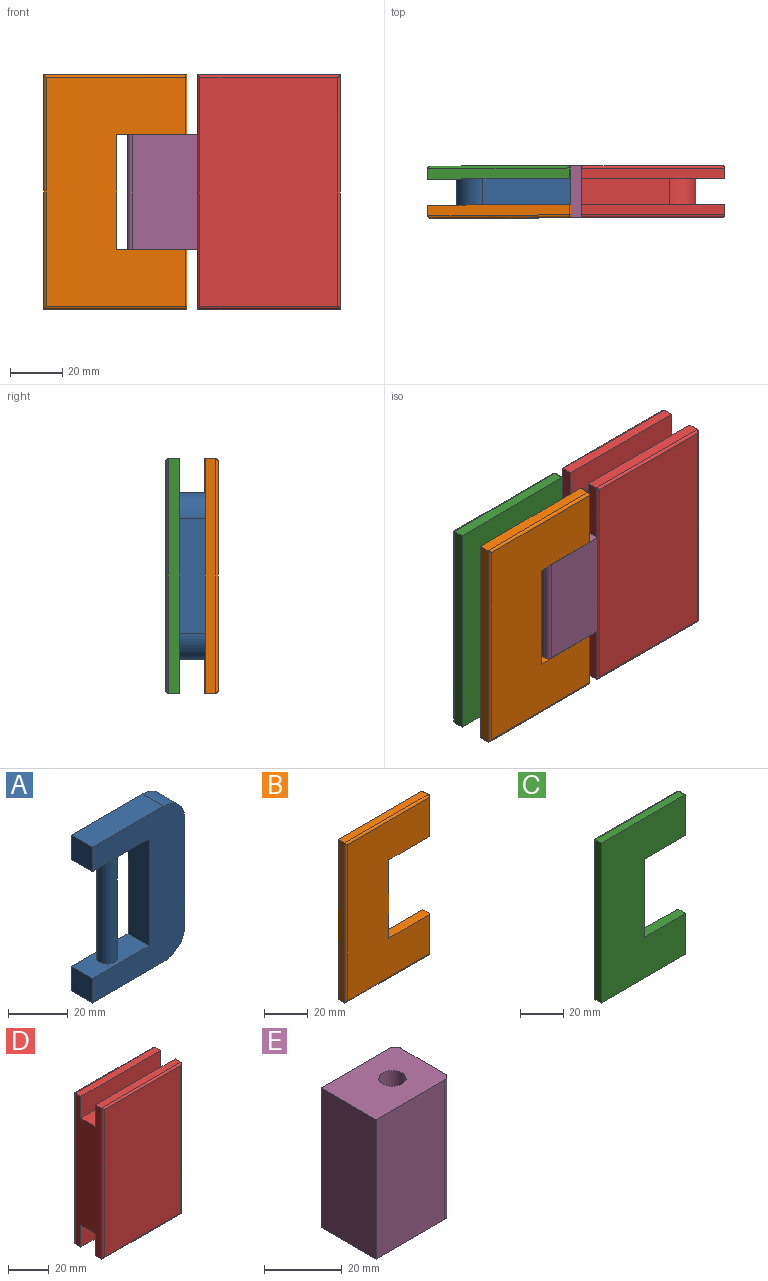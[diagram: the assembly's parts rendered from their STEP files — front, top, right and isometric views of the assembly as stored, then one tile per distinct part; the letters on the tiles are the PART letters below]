
ASSEMBLY  parts=5 mates=4
PART A: 13 faces, bbox 44x10x64 mm
  f0: plane 27x10mm, normal (0,0,-1), area 231.5mm2, adj f1,f9,f10,f11,f12
  f1: plane 44x10mm, normal (-1,0,0), area 440mm2, adj f0,f2,f10,f11
  f2: plane 27x10mm, normal (0,0,1), area 231.5mm2, adj f1,f3,f10,f11,f12
  f3: plane 10x10mm, normal (-1,0,0), area 100mm2, adj f2,f4,f10,f11
  f4: plane 34x10mm, normal (0,0,-1), area 340mm2, adj f3,f5,f10,f11
  f5: cylinder r=10mm len=10mm, axis (0,1,0), area 157.1mm2, adj f4,f6,f10,f11
  f6: plane 44x10mm, normal (1,0,0), area 440mm2, adj f5,f7,f10,f11
  f7: cylinder r=10mm len=10mm, axis (0,1,0), area 157.1mm2, adj f6,f8,f10,f11
  f8: plane 34x10mm, normal (0,0,1), area 340mm2, adj f7,f9,f10,f11
  f9: plane 10x10mm, normal (-1,0,0), area 100mm2, adj f0,f8,f10,f11
  f10: plane 64x44mm, normal (0,-1,0), area 1585.1mm2, adj f0,f1,f2,f3,f4,f5,f6,f7
  f11: plane 64x44mm, normal (0,1,0), area 1585.1mm2, adj f0,f1,f2,f3,f4,f5,f6,f7
  f12: cylinder r=3.5mm len=44mm, axis (0,0,-1), area 967.6mm2, adj f0,f2
PART B: 19 faces, bbox 55x5.1x90.2 mm
  f0: plane 90x4mm, normal (-1,0,0), area 360mm2, adj f1,f7,f9,f11
  f1: plane 54.5x4mm, normal (0,0,-1), area 218mm2, adj f0,f9,f12,f15
  f2: plane 22.5x4.5mm, normal (1,0,0), area 101.2mm2, adj f3,f9,f13,f14,f15
  f3: plane 27x5mm, normal (0,0,1), area 134.9mm2, adj f2,f4,f8,f9,f13
  f4: plane 44x5mm, normal (1,0,0), area 220mm2, adj f3,f5,f8,f9
  f5: plane 27x5mm, normal (0,0,-1), area 134.9mm2, adj f4,f6,f8,f9,f16
  f6: plane 22.5x4.5mm, normal (1,0,0), area 101.2mm2, adj f5,f9,f16,f17,f18
  f7: plane 54.5x4mm, normal (0,0,1), area 218mm2, adj f0,f9,f10,f18
  f8: plane 88x53.5mm, normal (0,-1,0), area 3542mm2, adj f3,f4,f5,f10,f11,f12,f13,f16
  f9: plane 90x55mm, normal (0,1,0), area 3761.9mm2, adj f0,f1,f2,f3,f4,f5,f6,f7
  f10: cylinder r=1mm len=54.5mm, axis (1,0,0), area 85mm2, adj f7,f8,f11,f17
  f11: cylinder r=1mm len=90mm, axis (0,0,1), area 140.2mm2, adj f0,f8,f10,f12
  f12: cylinder r=1mm len=54.5mm, axis (-1,0,0), area 85mm2, adj f1,f8,f11,f14
  f13: cylinder r=0.5mm len=22mm, axis (0,0,-1), area 17.3mm2, adj f2,f3,f8,f14
  f14: torus R=0.5mm, axis (-1,0,0), area 1mm2, adj f2,f12,f13,f15
  f15: cylinder r=0.5mm len=4mm, axis (0,1,0), area 3.1mm2, adj f1,f2,f9,f14
  f16: cylinder r=0.5mm len=22mm, axis (0,0,-1), area 17.3mm2, adj f5,f6,f8,f17
  f17: torus R=0.5mm, axis (-1,0,0), area 1mm2, adj f6,f10,f16,f18
  f18: cylinder r=0.5mm len=4mm, axis (0,-1,0), area 3.1mm2, adj f6,f7,f9,f17
PART C: 19 faces, bbox 55x5.1x90.2 mm
  f0: plane 90x4mm, normal (-1,0,0), area 360mm2, adj f1,f7,f9,f11
  f1: plane 54.5x4mm, normal (0,0,-1), area 218mm2, adj f0,f9,f12,f15
  f2: plane 22.5x4.5mm, normal (1,0,0), area 101.2mm2, adj f3,f9,f13,f14,f15
  f3: plane 27x5mm, normal (0,0,1), area 134.9mm2, adj f2,f4,f8,f9,f13
  f4: plane 44x5mm, normal (1,0,0), area 220mm2, adj f3,f5,f8,f9
  f5: plane 27x5mm, normal (0,0,-1), area 134.9mm2, adj f4,f6,f8,f9,f16
  f6: plane 22.5x4.5mm, normal (1,0,0), area 101.2mm2, adj f5,f9,f16,f17,f18
  f7: plane 54.5x4mm, normal (0,0,1), area 218mm2, adj f0,f9,f10,f18
  f8: plane 88x53.5mm, normal (0,1,0), area 3542mm2, adj f3,f4,f5,f10,f11,f12,f13,f16
  f9: plane 90x55mm, normal (0,-1,0), area 3761.9mm2, adj f0,f1,f2,f3,f4,f5,f6,f7
  f10: cylinder r=1mm len=54.5mm, axis (1,0,0), area 85mm2, adj f7,f8,f11,f17
  f11: cylinder r=1mm len=90mm, axis (0,0,1), area 140.2mm2, adj f0,f8,f10,f12
  f12: cylinder r=1mm len=54.5mm, axis (-1,0,0), area 85mm2, adj f1,f8,f11,f14
  f13: cylinder r=0.5mm len=22mm, axis (0,0,-1), area 17.3mm2, adj f2,f3,f8,f14
  f14: torus R=0.5mm, axis (-1,0,0), area 1mm2, adj f2,f12,f13,f15
  f15: cylinder r=0.5mm len=4mm, axis (0,-1,0), area 3.1mm2, adj f1,f2,f9,f14
  f16: cylinder r=0.5mm len=22mm, axis (0,0,-1), area 17.3mm2, adj f5,f6,f8,f17
  f17: torus R=0.5mm, axis (-1,0,0), area 1mm2, adj f6,f10,f16,f18
  f18: cylinder r=0.5mm len=4mm, axis (0,1,0), area 3.1mm2, adj f6,f7,f9,f17
PART D: 24 faces, bbox 55x20x90 mm
  f0: plane 90x55mm, normal (0,1,0), area 2176.9mm2, adj f1,f2,f3,f4,f19,f20,f21,f22
  f1: plane 90x18mm, normal (-1,0,0), area 1360mm2, adj f0,f2,f4,f6,f10,f12,f14,f15
  f2: plane 55x4mm, normal (0,0,-1), area 220mm2, adj f0,f1,f3,f7
  f3: plane 90x4mm, normal (1,0,0), area 360mm2, adj f0,f2,f4,f9
  f4: plane 55x4mm, normal (0,0,1), area 220mm2, adj f0,f1,f3,f8
  f5: plane 88x53mm, normal (0,-1,0), area 4664mm2, adj f6,f7,f8,f9
  f6: cylinder r=1mm len=90mm, axis (0,0,1), area 140.2mm2, adj f1,f5,f7,f8
  f7: cylinder r=1mm len=55mm, axis (-1,0,0), area 85.3mm2, adj f2,f5,f6,f9
  f8: cylinder r=1mm len=55mm, axis (1,0,0), area 85.3mm2, adj f4,f5,f6,f9
  f9: cylinder r=1mm len=90mm, axis (0,0,-1), area 140.2mm2, adj f3,f5,f7,f8
  f10: plane 55x4mm, normal (0,0,-1), area 220mm2, adj f1,f11,f14,f16
  f11: plane 90x4mm, normal (1,0,0), area 360mm2, adj f10,f12,f14,f18
  f12: plane 55x4mm, normal (0,0,1), area 220mm2, adj f1,f11,f14,f17
  f13: plane 88x53mm, normal (0,1,0), area 4664mm2, adj f15,f16,f17,f18
  f14: plane 90x55mm, normal (0,-1,0), area 2176.9mm2, adj f1,f10,f11,f12,f19,f20,f21,f22
  f15: cylinder r=1mm len=90mm, axis (0,0,1), area 140.2mm2, adj f1,f13,f16,f17
  f16: cylinder r=1mm len=55mm, axis (-1,0,0), area 85.3mm2, adj f10,f13,f15,f18
  f17: cylinder r=1mm len=55mm, axis (1,0,0), area 85.3mm2, adj f12,f13,f15,f18
  f18: cylinder r=1mm len=90mm, axis (0,0,-1), area 140.2mm2, adj f11,f13,f16,f17
  f19: plane 34x10mm, normal (0,0,1), area 340mm2, adj f0,f1,f14,f23
  f20: plane 34x10mm, normal (0,0,-1), area 340mm2, adj f0,f1,f14,f21
  f21: cylinder r=10mm len=10mm, axis (0,1,0), area 157.1mm2, adj f0,f14,f20,f22
  f22: plane 44x10mm, normal (1,0,0), area 440mm2, adj f0,f14,f21,f23
  f23: cylinder r=10mm len=10mm, axis (0,1,0), area 157.1mm2, adj f0,f14,f19,f22
PART E: 9 faces, bbox 27x20x44 mm
  f0: plane 44x25mm, normal (0,1,0), area 1100mm2, adj f1,f5,f7,f8
  f1: plane 44x20mm, normal (-1,0,0), area 880mm2, adj f0,f2,f7,f8
  f2: plane 44x25mm, normal (0,-1,0), area 1100mm2, adj f1,f3,f7,f8
  f3: cylinder r=2mm len=44mm, axis (0,0,-1), area 138.2mm2, adj f2,f4,f7,f8
  f4: plane 44x16mm, normal (1,0,0), area 704mm2, adj f3,f5,f7,f8
  f5: cylinder r=2mm len=44mm, axis (0,0,-1), area 138.2mm2, adj f0,f4,f7,f8
  f6: cylinder r=3.5mm len=44mm, axis (0,0,-1), area 967.6mm2, adj f7,f8
  f7: plane 27x20mm, normal (0,0,1), area 499.8mm2, adj f0,f1,f2,f3,f4,f5,f6
  f8: plane 27x20mm, normal (0,0,-1), area 499.8mm2, adj f0,f1,f2,f3,f4,f5,f6
PLACE A rot(axis=(0,0,-1),179.7deg) t=(-31.65,20.83,-0.72)mm
PLACE B rot(axis=(0,0,1),0.3deg) t=(-86.65,20.52,-13.72)mm
PLACE C rot(axis=(0,0,1),0.3deg) t=(-86.65,20.52,-13.72)mm
PLACE D t=(-27.65,20.76,-13.72)mm fixed
PLACE E rot(axis=(0,0,-1),180deg) t=(-27.65,20.76,9.28)mm
MATE revolute E.f6 <-> A.f12  axis (0,0,1) through (-43.65,20.76,53.28)mm
MATE fastened B.f6 <-> A.f9  axis (-1,-0.01,0) through (-31.63,15.83,53.28)mm
MATE fastened D.f1 <-> E.f1  axis (-1,0,0) through (-27.65,20.76,31.28)mm
MATE fastened C.f6 <-> A.f9  axis (-1,-0.01,0) through (-31.68,25.83,53.28)mm
